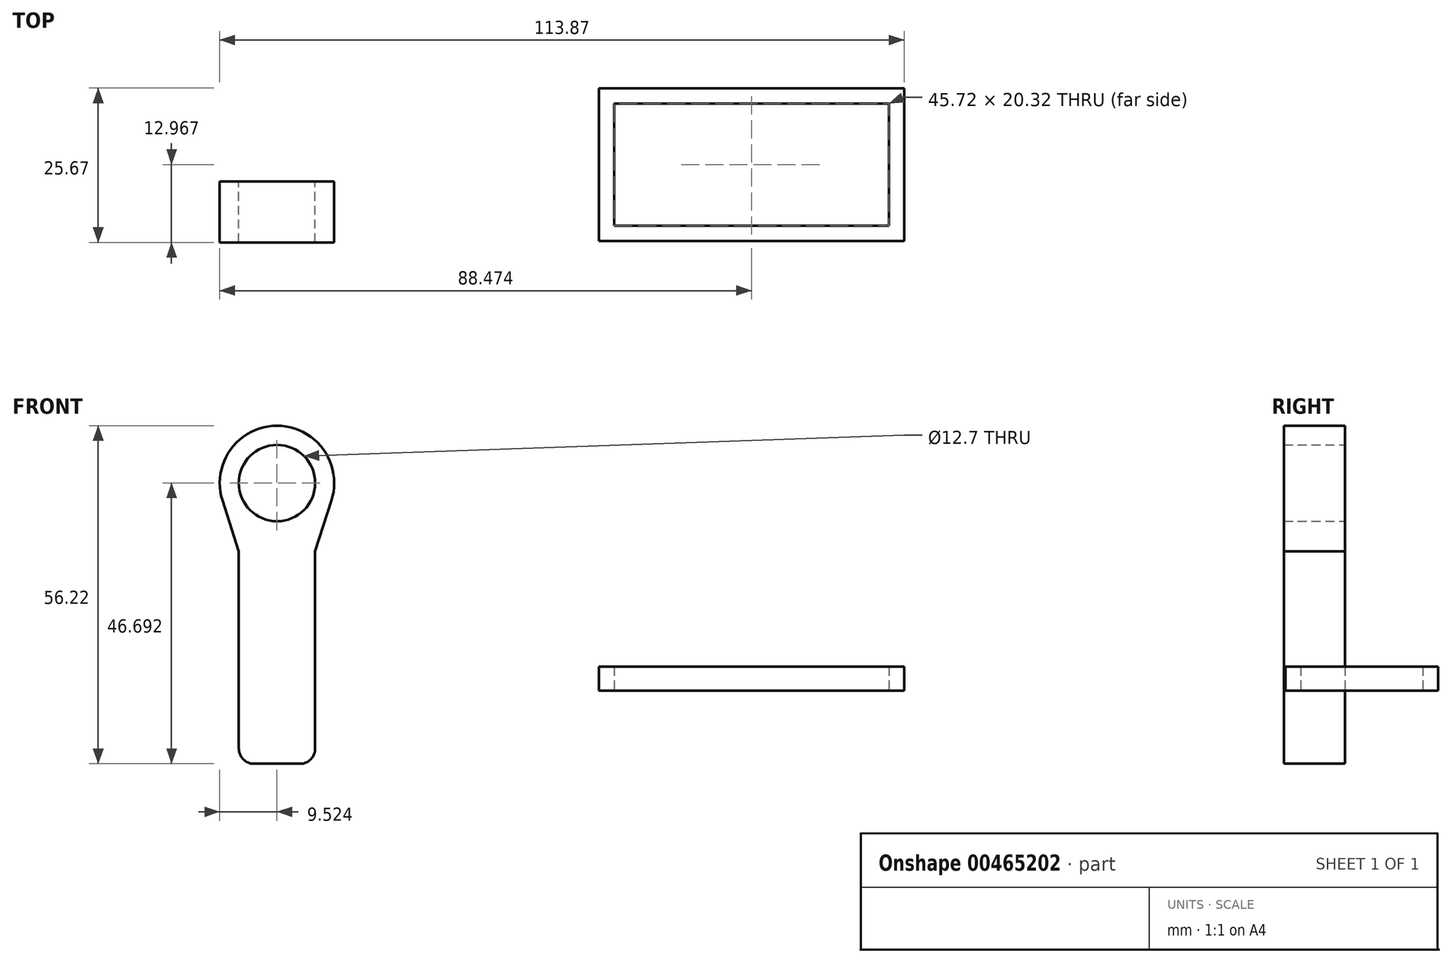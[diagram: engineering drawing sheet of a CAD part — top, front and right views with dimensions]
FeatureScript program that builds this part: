
annotation { "Feature Type Name" : "Feature", "Feature Type Description" : "" }
export const myFeature = defineFeature(function(context is Context, id is Id, definition is map)
    precondition{}
    {
        {
            assignVariable(context, id + "F0", {"name" : "SupportHeight", "anyValue" : 4});
        }
        {
            var Q0;
            Q0=qCreatedBy(makeId("Top.planeOp"),FACE);
            var sketch = newSketch(context, id + "F1", { "sketchPlane" : qUnion([Q0])});
            skLineSegment(sketch, "E0.bottom", {"start": v(-12.75, 15.5) * mm, "end": v(38.05, 15.5) * mm});
            skLineSegment(sketch, "E0.top", {"start": v(-12.75, -9.9) * mm, "end": v(38.05, -9.9) * mm});
            skLineSegment(sketch, "E0.left", {"start": v(-12.75, 15.5) * mm, "end": v(-12.75, -9.9) * mm});
            skLineSegment(sketch, "E0.right", {"start": v(38.05, 15.5) * mm, "end": v(38.05, -9.9) * mm});
            skLineSegment(sketch, "E1.bottom", {"start": v(-10.2, 12.97) * mm, "end": v(35.51, 12.97) * mm});
            skLineSegment(sketch, "E1.top", {"start": v(-10.2, -7.35) * mm, "end": v(35.51, -7.35) * mm});
            skLineSegment(sketch, "E1.left", {"start": v(-10.2, 12.97) * mm, "end": v(-10.2, -7.35) * mm});
            skLineSegment(sketch, "E1.right", {"start": v(35.51, 12.97) * mm, "end": v(35.51, -7.35) * mm});
            skSolve(sketch);
        }
        {
            var Q0;
            Q0=makeQuery(id+"F1.imprint","IMPRINT",FACE,{"disambiguationData":[TD([[makeQuery(id+"F1.imprint","IMPRINT",EDGE,{"derivedFrom":sQuery(id+"F1.wireOp",EDGE,"E0.bottom")}),-1.0]])]});
            extrude(context, id + "F2", {"entities" : qUnion([Q0]), "depth" : (getVariable(context, 'SupportHeight')) * mm});
        }
        {
            var Q0;
            Q0=makeQuery(id+"F2.opExtrude","SWEPT_FACE",FACE,{"disambiguationData":[OSD([sQuery(id+"F1.wireOp",EDGE,"E0.top")])]});
            var sketch = newSketch(context, id + "F3", { "sketchPlane" : qUnion([Q0])});
            skCircle(sketch, "E2", {"center": v(12.65, 76.2) * mm, "radius": 12.7 * mm});
            skLineSegment(sketch, "E3", {"start": v(12.65, 101.6) * mm, "end": v(12.65, 0) * mm, "construction": true});
            skSolve(sketch);
        }
        {
            var Q0;
            Q0=makeQuery(id+"F3.imprint","IMPRINT",FACE,{"disambiguationData":[TD([[makeQuery(id+"F3.imprint","IMPRINT",EDGE,{"derivedFrom":sQuery(id+"F3.wireOp",EDGE,"E2")}),1.0]])]});
            var Q1;
            Q1=makeQuery(id+"F2.opExtrude","SWEPT_FACE",FACE,{"disambiguationData":[OSD([sQuery(id+"F1.wireOp",EDGE,"E0.bottom")])]});
            extrude(context, id + "F4", {"entities" : qUnion([Q0]), "operationType" : NewBodyOperationType.REMOVE, "endBound" : BoundingType.UP_TO_SURFACE, "oppositeDirection" : true, "endBoundEntityFace" : qUnion([Q1]), "depth" : 25.4 * mm});
        }
        {
            var Q0;
            Q0=qCreatedBy(makeId("Front.planeOp"),FACE);
            var sketch = newSketch(context, id + "F5", { "sketchPlane" : qUnion([Q0])});
            skLineSegment(sketch, "E4", {"start": v(-72.65, 23.2) * mm, "end": v(-72.65, -9.62) * mm});
            skLineSegment(sketch, "E5", {"start": v(-59.95, 23.2) * mm, "end": v(-59.95, -9.62) * mm});
            skLineSegment(sketch, "E6", {"start": v(-70.1, -12.16) * mm, "end": v(-62.49, -12.16) * mm});
            skPoint(sketch, "E7.visualSharp", {"position": v(-72.65, -12.16) * mm});
            skArc(sketch, "E7.filletArc", {"start": v(-72.65, -9.62) * mm, "mid": v(-71.9, -11.42) * mm, "end": v(-70.1, -12.16) * mm});
            skPoint(sketch, "E8.visualSharp", {"position": v(-59.95, -12.16) * mm});
            skArc(sketch, "E8.filletArc", {"start": v(-62.49, -12.16) * mm, "mid": v(-60.69, -11.42) * mm, "end": v(-59.95, -9.62) * mm});
            skCircle(sketch, "E9", {"center": v(-66.3, 34.53) * mm, "radius": 6.35 * mm});
            skPoint(sketch, "E10", {"position": v(-66.3, -12.16) * mm});
            skCircle(sketch, "E11", {"center": v(-66.3, 34.53) * mm, "radius": 9.53 * mm});
            skLineSegment(sketch, "E12", {"start": v(-57.23, 31.6) * mm, "end": v(-59.95, 23.2) * mm});
            skLineSegment(sketch, "E13", {"start": v(-72.65, 23.2) * mm, "end": v(-75.36, 31.6) * mm});
            skSolve(sketch);
        }
        {
            var Q0;
            Q0=makeQuery(id+"F5.imprint","IMPRINT",FACE,{"disambiguationData":[TD([[makeQuery(id+"F5.imprint","IMPRINT",EDGE,{"derivedFrom":sQuery(id+"F5.wireOp",EDGE,"E9")}),-1.0]])]});
            var Q1;
            Q1=makeQuery(id+"F5.imprint","IMPRINT",FACE,{"disambiguationData":[TD([[makeQuery(id+"F5.imprint","IMPRINT",EDGE,{"derivedFrom":sQuery(id+"F5.wireOp",EDGE,"E4")}),1.0]])]});
            extrude(context, id + "F6", {"entities" : qUnion([Q0, Q1]), "depth" : 10.16 * mm});
        }
    });
